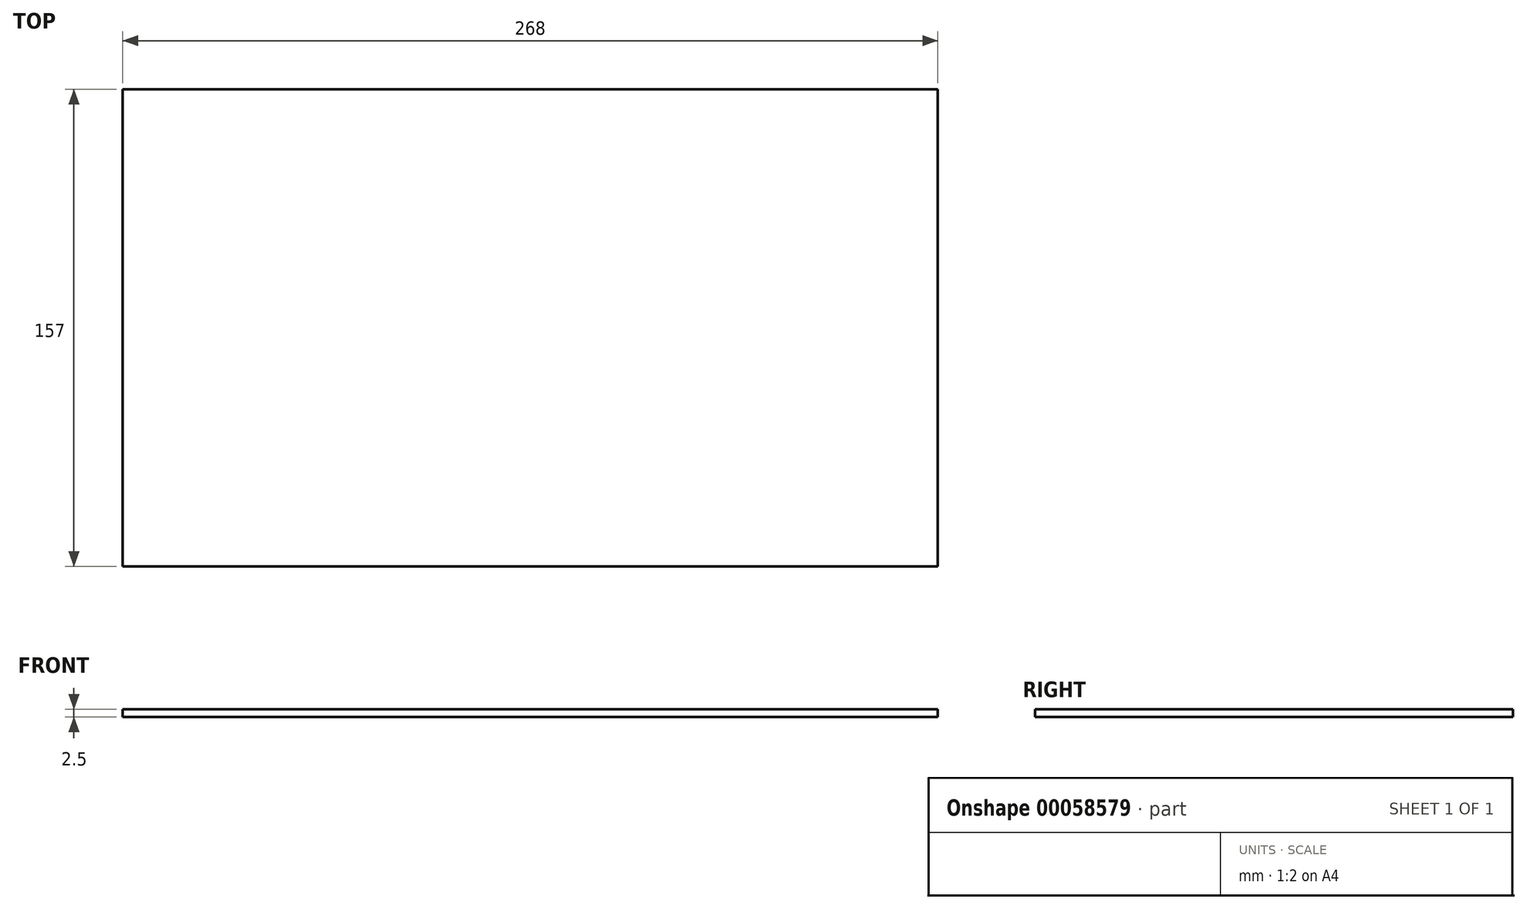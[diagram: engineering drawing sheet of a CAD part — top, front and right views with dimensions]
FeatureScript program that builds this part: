
annotation { "Feature Type Name" : "Feature", "Feature Type Description" : "" }
export const myFeature = defineFeature(function(context is Context, id is Id, definition is map)
    precondition{}
    {
        {
            var Q0;
            Q0=qCreatedBy(makeId("Top.planeOp"),FACE);
            var sketch = newSketch(context, id + "F0", { "sketchPlane" : qUnion([Q0])});
            skLineSegment(sketch, "E0.bottom", {"start": v(-135, 76) * mm, "end": v(133, 76) * mm});
            skLineSegment(sketch, "E0.top", {"start": v(-135, -81) * mm, "end": v(133, -81) * mm});
            skLineSegment(sketch, "E0.left", {"start": v(-135, 76) * mm, "end": v(-135, -81) * mm});
            skLineSegment(sketch, "E0.right", {"start": v(133, 76) * mm, "end": v(133, -81) * mm});
            skLineSegment(sketch, "E1.rect.bottom", {"start": v(128.5, 72.5) * mm, "end": v(-128.5, 72.5) * mm});
            skLineSegment(sketch, "E1.rect.top", {"start": v(128.5, -72.5) * mm, "end": v(-128.5, -72.5) * mm});
            skLineSegment(sketch, "E1.rect.left", {"start": v(128.5, 72.5) * mm, "end": v(128.5, -72.5) * mm});
            skLineSegment(sketch, "E1.rect.right", {"start": v(-128.5, 72.5) * mm, "end": v(-128.5, -72.5) * mm});
            skPoint(sketch, "E1.rect.middle", {"position": v(0, 0) * mm});
            skLineSegment(sketch, "E2.bottom", {"start": v(-91.5, -81) * mm, "end": v(113.5, -81) * mm});
            skLineSegment(sketch, "E2.top", {"start": v(-91.5, -90) * mm, "end": v(113.5, -90) * mm});
            skLineSegment(sketch, "E2.left", {"start": v(-91.5, -81) * mm, "end": v(-91.5, -90) * mm});
            skLineSegment(sketch, "E2.right", {"start": v(113.5, -81) * mm, "end": v(113.5, -90) * mm});
            skSolve(sketch);
        }
        {
            var Q0;
            Q0=makeQuery(id+"F0.imprint","IMPRINT",FACE,{"disambiguationData":[TD([[makeQuery(id+"F0.imprint","IMPRINT",EDGE,{"derivedFrom":sQuery(id+"F0.wireOp",EDGE,"E1.rect.bottom")}),1.0]])]});
            var Q1;
            Q1=makeQuery(id+"F0.imprint","IMPRINT",FACE,{"disambiguationData":[TD([[makeQuery(id+"F0.imprint","IMPRINT",EDGE,{"derivedFrom":sQuery(id+"F0.wireOp",EDGE,"E0.bottom")}),-1.0]])]});
            var Q2;
            Q2=makeQuery(id+"F0.imprint","IMPRINT",FACE,{"disambiguationData":[TD([[makeQuery(id+"F0.imprint","IMPRINT",EDGE,{"derivedFrom":sQuery(id+"F0.wireOp",EDGE,"E2.bottom")}),-1.0]])]});
            extrude(context, id + "F1", {"entities" : qUnion([Q0, Q1, Q2]), "depth" : 2.5 * mm});
        }
        {
            var Q0;
            Q0=makeQuery(id+"F1.opExtrude","CAP_FACE",FACE,{"disambiguationData":[OSD([sQuery(id+"F0.wireOp",EDGE,"E0.bottom"),sQuery(id+"F0.wireOp",EDGE,"E0.top"),sQuery(id+"F0.wireOp",EDGE,"E0.left"),sQuery(id+"F0.wireOp",EDGE,"E0.right"),sQuery(id+"F0.wireOp",EDGE,"E2.top"),sQuery(id+"F0.wireOp",EDGE,"E2.left"),sQuery(id+"F0.wireOp",EDGE,"E2.right")])],"isStart":false});
            var sketch = newSketch(context, id + "F2", { "sketchPlane" : qUnion([Q0])});
            skLineSegment(sketch, "E3.bottom", {"start": v(-46.5, -90) * mm, "end": v(-26.5, -90) * mm});
            skLineSegment(sketch, "E3.top", {"start": v(-46.5, -82.3) * mm, "end": v(-26.5, -82.3) * mm});
            skLineSegment(sketch, "E3.left", {"start": v(-46.5, -90) * mm, "end": v(-46.5, -82.3) * mm});
            skLineSegment(sketch, "E3.right", {"start": v(-26.5, -90) * mm, "end": v(-26.5, -82.3) * mm});
            skPoint(sketch, "E4", {"position": v(-36.5, -82.3) * mm});
            skPoint(sketch, "E5", {"position": v(-36.5, -90) * mm});
            skPoint(sketch, "E6", {"position": v(-46.5, -86.15) * mm});
            skSolve(sketch);
        }
        {
            var Q0;
            Q0 = qSketchRegion(id + "F2", true);
            extrude(context, id + "F3", {"entities" : qUnion([Q0]), "operationType" : NewBodyOperationType.REMOVE, "oppositeDirection" : true, "depth" : 0.5 * mm});
        }
    });
